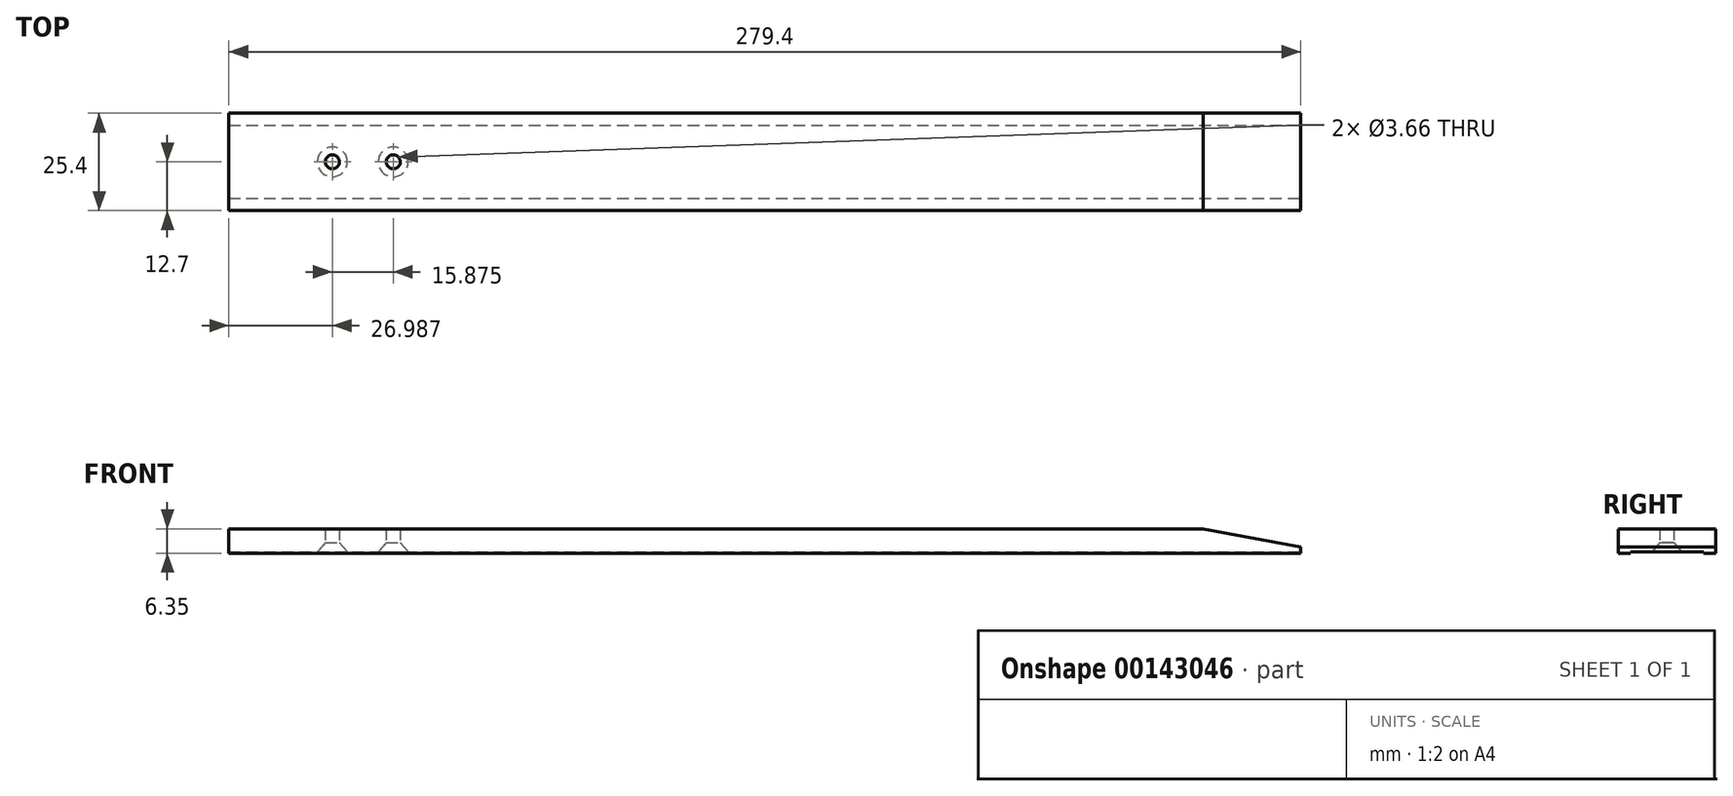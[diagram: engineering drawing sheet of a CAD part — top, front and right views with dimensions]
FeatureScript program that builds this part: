
annotation { "Feature Type Name" : "Feature", "Feature Type Description" : "" }
export const myFeature = defineFeature(function(context is Context, id is Id, definition is map)
    precondition{}
    {
        {
            var Q0;
            Q0=qCreatedBy(makeId("Top.planeOp"),FACE);
            var sketch = newSketch(context, id + "F0", { "sketchPlane" : qUnion([Q0])});
            skLineSegment(sketch, "E0.bottom", {"start": v(-139.7, 12.7) * mm, "end": v(139.7, 12.7) * mm});
            skLineSegment(sketch, "E0.top", {"start": v(-139.7, -12.7) * mm, "end": v(139.7, -12.7) * mm});
            skLineSegment(sketch, "E0.left", {"start": v(-139.7, 12.7) * mm, "end": v(-139.7, -12.7) * mm});
            skLineSegment(sketch, "E0.right", {"start": v(139.7, 12.7) * mm, "end": v(139.7, -12.7) * mm});
            skPoint(sketch, "E0.middle", {"position": v(0, 0) * mm});
            skSolve(sketch);
        }
        {
            var Q0;
            Q0 = qSketchRegion(id + "F0", true);
            extrude(context, id + "F1", {"entities" : qUnion([Q0]), "endBound" : BoundingType.SYMMETRIC, "depth" : 6.35 * mm});
        }
        {
            var Q0;
            Q0=makeQuery(id+"F1.opExtrude","SWEPT_FACE",FACE,{"disambiguationData":[OSD([sQuery(id+"F0.wireOp",EDGE,"E0.top")])]});
            var sketch = newSketch(context, id + "F2", { "sketchPlane" : qUnion([Q0])});
            skLineSegment(sketch, "E1", {"start": v(114.3, 3.18) * mm, "end": v(139.7, 3.18) * mm});
            skLineSegment(sketch, "E2", {"start": v(139.7, 3.18) * mm, "end": v(139.7, -1.59) * mm});
            skLineSegment(sketch, "E3", {"start": v(139.7, -1.59) * mm, "end": v(114.3, 3.17) * mm});
            skSolve(sketch);
        }
        {
            var Q0;
            Q0 = qSketchRegion(id + "F2", true);
            extrude(context, id + "F3", {"entities" : qUnion([Q0]), "operationType" : NewBodyOperationType.REMOVE, "oppositeDirection" : true, "depth" : 25.4 * mm});
        }
        {
            var Q0;
            Q0=makeQuery(id+"F1.opExtrude","CAP_FACE",FACE,{"disambiguationData":[OSD([sQuery(id+"F0.wireOp",EDGE,"E0.bottom"),sQuery(id+"F0.wireOp",EDGE,"E0.top"),sQuery(id+"F0.wireOp",EDGE,"E0.left"),sQuery(id+"F0.wireOp",EDGE,"E0.right")])],"isStart":true});
            var sketch = newSketch(context, id + "F4", { "sketchPlane" : qUnion([Q0])});
            skLineSegment(sketch, "E4.bottom", {"start": v(-139.7, 9.52) * mm, "end": v(139.7, 9.52) * mm});
            skLineSegment(sketch, "E4.top", {"start": v(-139.7, -9.53) * mm, "end": v(139.7, -9.53) * mm});
            skLineSegment(sketch, "E4.left", {"start": v(-139.7, 9.52) * mm, "end": v(-139.7, -9.53) * mm});
            skLineSegment(sketch, "E4.right", {"start": v(139.7, 9.52) * mm, "end": v(139.7, -9.53) * mm});
            skPoint(sketch, "E4.middle", {"position": v(0, 0) * mm});
            skSolve(sketch);
        }
        {
            var Q0;
            Q0 = qSketchRegion(id + "F4", true);
            extrude(context, id + "F5", {"entities" : qUnion([Q0]), "operationType" : NewBodyOperationType.REMOVE, "oppositeDirection" : true, "depth" : 0.32 * mm});
        }
        {
            var Q0;
            Q0=makeQuery(id+"F5.boolean.opBoolean","COPY",FACE,{"derivedFrom":makeQuery(id+"F5.opExtrude","CAP_FACE",FACE,{"disambiguationData":[OSD([sQuery(id+"F4.wireOp",EDGE,"E4.bottom"),sQuery(id+"F4.wireOp",EDGE,"E4.top"),sQuery(id+"F4.wireOp",EDGE,"E4.left"),sQuery(id+"F4.wireOp",EDGE,"E4.right")])],"isStart":false})});
            var sketch = newSketch(context, id + "F6", { "sketchPlane" : qUnion([Q0])});
            skLineSegment(sketch, "E5", {"start": v(-112.71, 0) * mm, "end": v(-96.84, 0) * mm, "construction": true});
            skCircle(sketch, "E6", {"center": v(-112.71, 0) * mm, "radius": 1.83 * mm});
            skCircle(sketch, "E7", {"center": v(-96.84, 0) * mm, "radius": 1.83 * mm});
            skSolve(sketch);
        }
        {
            var Q0;
            Q0=sQuery(id+"F6.wireOp",VERTEX,"E5.start");
            var Q1;
            Q1=sQuery(id+"F6.wireOp",VERTEX,"E7.center");
            var Q2;
            Q2=makeQuery(id+"F1.opExtrude","SWEPT_BODY",BODY,{"disambiguationData":[OSD([sQuery(id+"F0.wireOp",EDGE,"E0.bottom"),sQuery(id+"F0.wireOp",EDGE,"E0.top"),sQuery(id+"F0.wireOp",EDGE,"E0.left"),sQuery(id+"F0.wireOp",EDGE,"E0.right")])]});
            hole(context, id + "F7", {"style" : HoleStyle.C_SINK, "endStyle" : HoleEndStyle.THROUGH, "standardTappedOrClearance" : lookupTablePath({ "standard" : "ANSI", "fit" : "Close", "size" : "#6", "type" : "Clearance" }), "standardBlindInLast" : lookupTablePath({ "fit" : "Close", "standard" : "ANSI", "size" : "#6", "type" : "Clearance" }), "holeDiameter" : 3.66 * mm, "cSinkDiameter" : 7.8 * mm, "cSinkAngle" : 82 * degree, "locations" : qUnion([Q0, Q1]), "scope" : qUnion([Q2]), "isTappedThrough" : true});
        }
    });
